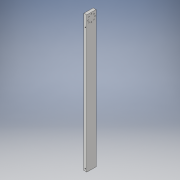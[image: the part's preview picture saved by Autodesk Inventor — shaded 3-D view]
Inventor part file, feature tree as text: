
AUTODESK INVENTOR PART (.ipt)
format: ipt  version: 2017 (Build 210142000, 142)  size: 128,512 bytes
history: native  units: in
note: dims shown in document units (in); Inventor stores cm internally (conversion verified against a paired STEP export)
features: sketch x3, hole x2, extrude x1
ambient origin geometry x8: Origin, YZ Plane, XZ Plane, XY Plane, X Axis, Y Axis, Z Axis, Center Point
bodies: Solid1 (feature_tree)
feature tree (6):
  extrude  "Extrusion1"  Depth=14.75in
  sketch  "Sketch2"  dims[d2=1.0in d3=0.0in d4=0.25in]
  hole  "Hole1"  [1 undecoded]
  hole  "Hole2"  [1 undecoded]
  sketch  "Sketch1"  dims[d0=0.312in d1=14.75in]
  sketch  "Sketch3"  dims[d5=0.14in d6=1.25in d7=0.14in d10=0.104in d11=1.0in d12=0.375in d13=0.25in d14=0.5635in d15=1.0in d16=0.8108in d24=0.107in d25=0.3in d26=0.375in d27=0.25in d28=0.5635in d29=1.0in d30=0.8108in d35=0.55in d36=0.77in d37=3.1496in d39=360.0deg]
note: 2 required parameter values undecoded (feature->parameter linkage not recoverable at this tier; creation-order binding heuristic only, values carry confidence <= 0.55)
